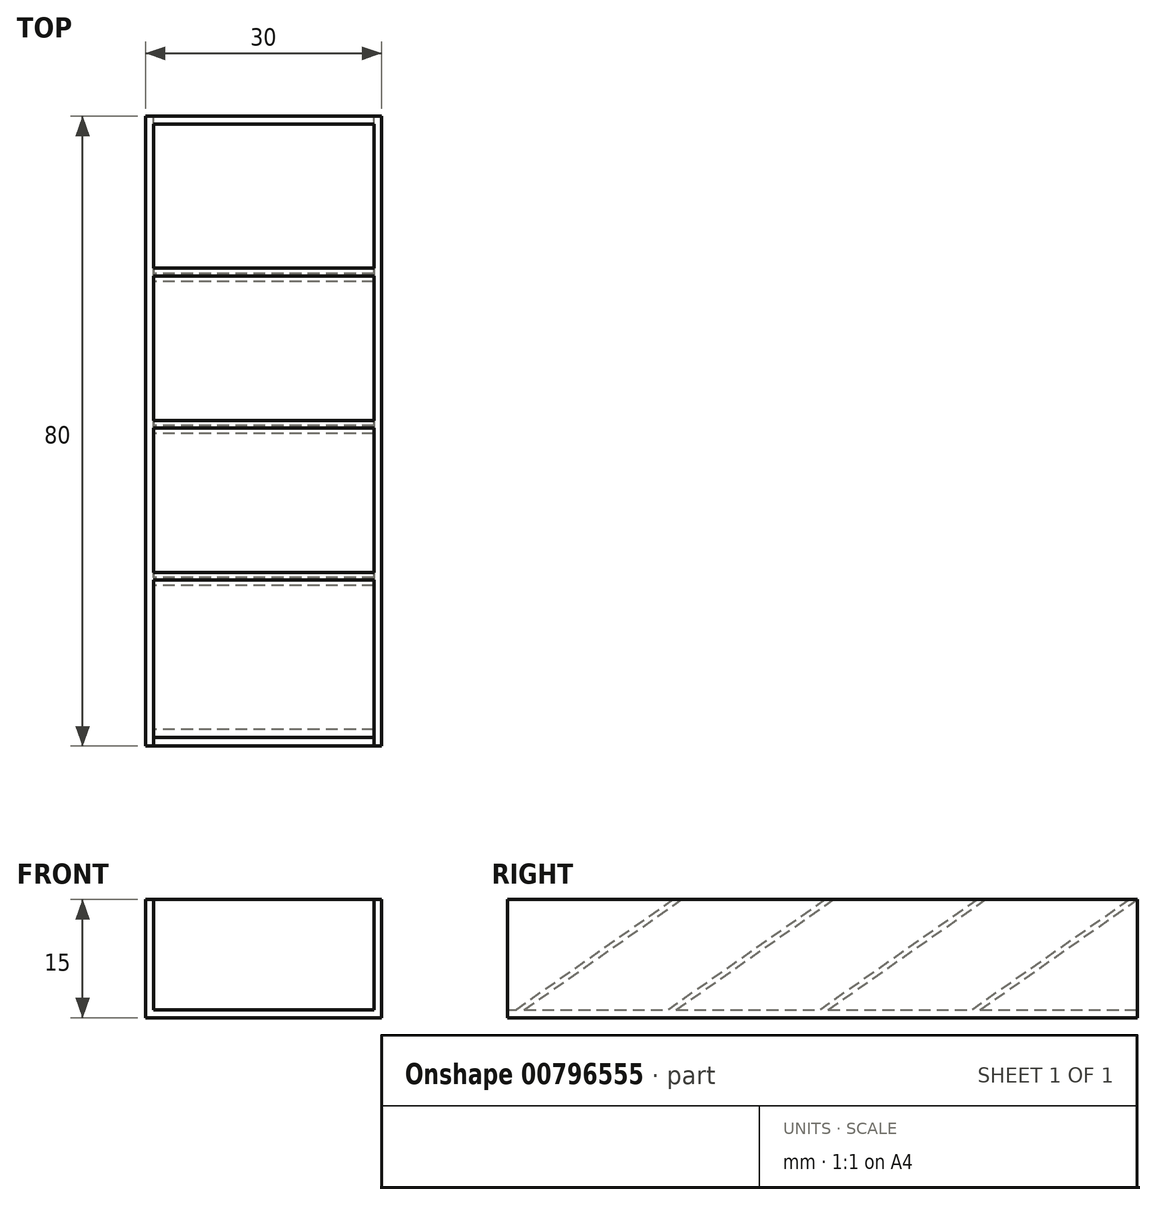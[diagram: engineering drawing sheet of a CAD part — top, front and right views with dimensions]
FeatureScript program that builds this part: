
annotation { "Feature Type Name" : "Feature", "Feature Type Description" : "" }
export const myFeature = defineFeature(function(context is Context, id is Id, definition is map)
    precondition{}
    {
        {
            var Q0;
            Q0=qCreatedBy(makeId("Top.planeOp"),FACE);
            var sketch = newSketch(context, id + "F0", { "sketchPlane" : qUnion([Q0])});
            skLineSegment(sketch, "E0.bottom", {"start": v(15, -40) * mm, "end": v(-15, -40) * mm});
            skLineSegment(sketch, "E0.top", {"start": v(15, 40) * mm, "end": v(-15, 40) * mm});
            skLineSegment(sketch, "E0.left", {"start": v(15, -40) * mm, "end": v(15, 40) * mm});
            skLineSegment(sketch, "E0.right", {"start": v(-15, -40) * mm, "end": v(-15, 40) * mm});
            skPoint(sketch, "E0.middle", {"position": v(0, 0) * mm});
            skLineSegment(sketch, "E1", {"start": v(-14, 40) * mm, "end": v(-14, -40) * mm});
            skLineSegment(sketch, "E2", {"start": v(14, 40) * mm, "end": v(14, -40) * mm});
            skSolve(sketch);
        }
        {
            var Q0;
            Q0=makeQuery(id+"F0.imprint","IMPRINT",FACE,{"disambiguationData":[TD([[makeQuery(id+"F0.imprint","IMPRINT",EDGE,{"derivedFrom":sQuery(id+"F0.wireOp",EDGE,"E0.bottom")}),-1.0]])]});
            extrude(context, id + "F1", {"entities" : qUnion([Q0]), "depth" : 1 * mm, "offsetDistance" : 25 * mm});
        }
        {
            var Q0;
            {var subQ0=sQuery(id+"F0.wireOp",EDGE,"E0.right");Q0=makeQuery(id+"F0.imprint","IMPRINT",FACE,{"disambiguationData":[TD([[makeQuery(id+"F0.imprint","IMPRINT",EDGE,{"derivedFrom":subQ0}),-1.0]])]});}
            var Q1;
            {var subQ0=sQuery(id+"F0.wireOp",EDGE,"E0.left");Q1=makeQuery(id+"F0.imprint","IMPRINT",FACE,{"disambiguationData":[TD([[makeQuery(id+"F0.imprint","IMPRINT",EDGE,{"derivedFrom":subQ0}),1.0]])]});}
            extrude(context, id + "F2", {"entities" : qUnion([Q0, Q1]), "operationType" : NewBodyOperationType.ADD, "depth" : 15 * mm, "offsetDistance" : 25 * mm});
        }
        {
            var Q0;
            Q0=makeQuery(id+"F2.opExtrude","SWEPT_FACE",FACE,{"disambiguationData":[OSD([sQuery(id+"F0.wireOp",EDGE,"E1")])]});
            var sketch = newSketch(context, id + "F3", { "sketchPlane" : qUnion([Q0])});
            skLineSegment(sketch, "E3", {"start": v(20, 1) * mm, "end": v(40, 15) * mm});
            skLineSegment(sketch, "E4", {"start": v(40, 15) * mm, "end": v(39, 15) * mm});
            skLineSegment(sketch, "E5", {"start": v(39, 15) * mm, "end": v(19, 1) * mm});
            skLineSegment(sketch, "E6", {"start": v(19, 1) * mm, "end": v(20, 1) * mm});
            skLineSegment(sketch, "E7.1.0.0", {"start": v(19.7, 15) * mm, "end": v(-0.3, 1) * mm});
            skLineSegment(sketch, "E7.1.0.1", {"start": v(20.7, 15) * mm, "end": v(19.7, 15) * mm});
            skLineSegment(sketch, "E7.1.0.2", {"start": v(0.7, 1) * mm, "end": v(20.7, 15) * mm});
            skLineSegment(sketch, "E7.1.0.3", {"start": v(-0.3, 1) * mm, "end": v(0.7, 1) * mm});
            skLineSegment(sketch, "E7.2.0.0", {"start": v(0.39, 15) * mm, "end": v(-19.6, 1) * mm});
            skLineSegment(sketch, "E7.2.0.1", {"start": v(1.39, 15) * mm, "end": v(0.39, 15) * mm});
            skLineSegment(sketch, "E7.2.0.2", {"start": v(-18.6, 1) * mm, "end": v(1.39, 15) * mm});
            skLineSegment(sketch, "E7.2.0.3", {"start": v(-19.6, 1) * mm, "end": v(-18.6, 1) * mm});
            skLineSegment(sketch, "E7.direction1", {"start": v(19, 1) * mm, "end": v(-0.3, 1) * mm, "construction": true});
            skLineSegment(sketch, "E8.0.3.0", {"start": v(-18.92, 15) * mm, "end": v(-38.91, 1) * mm});
            skLineSegment(sketch, "E8.3.3.0", {"start": v(-17.92, 15) * mm, "end": v(-18.92, 15) * mm});
            skLineSegment(sketch, "E8.6.3.0", {"start": v(-37.91, 1) * mm, "end": v(-17.92, 15) * mm});
            skLineSegment(sketch, "E8.9.3.0", {"start": v(-38.91, 1) * mm, "end": v(-37.91, 1) * mm});
            skSolve(sketch);
        }
        {
            var Q0;
            Q0=makeQuery(id+"F3.imprint","IMPRINT",FACE,{"disambiguationData":[TD([[makeQuery(id+"F3.imprint","IMPRINT",EDGE,{"derivedFrom":sQuery(id+"F3.wireOp",EDGE,"E3")}),1.0]])]});
            var Q1;
            Q1=makeQuery(id+"F3.imprint","IMPRINT",FACE,{"disambiguationData":[TD([[makeQuery(id+"F3.imprint","IMPRINT",EDGE,{"derivedFrom":sQuery(id+"F3.wireOp",EDGE,"E7.1.0.0")}),1.0]])]});
            var Q2;
            Q2=makeQuery(id+"F3.imprint","IMPRINT",FACE,{"disambiguationData":[TD([[makeQuery(id+"F3.imprint","IMPRINT",EDGE,{"derivedFrom":sQuery(id+"F3.wireOp",EDGE,"E7.2.0.0")}),1.0]])]});
            var Q3;
            Q3=makeQuery(id+"F3.imprint","IMPRINT",FACE,{"disambiguationData":[TD([[makeQuery(id+"F3.imprint","IMPRINT",EDGE,{"derivedFrom":sQuery(id+"F3.wireOp",EDGE,"E8.0.3.0")}),1.0]])]});
            extrude(context, id + "F4", {"entities" : qUnion([Q0, Q1, Q2, Q3]), "operationType" : NewBodyOperationType.ADD, "endBound" : BoundingType.UP_TO_NEXT, "depth" : 25 * mm, "offsetDistance" : 25 * mm});
        }
    });
